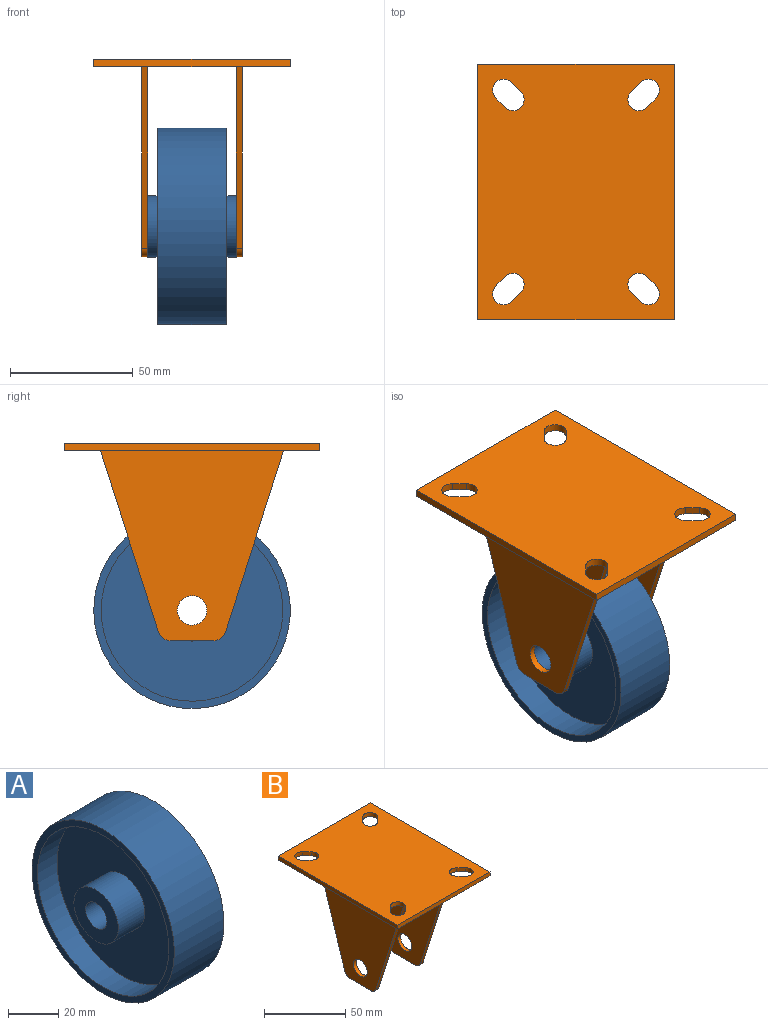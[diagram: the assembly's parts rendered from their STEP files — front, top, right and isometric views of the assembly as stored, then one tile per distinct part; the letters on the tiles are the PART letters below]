
ASSEMBLY  parts=2 mates=1
PART A: 12 faces, bbox 36x80x80 mm
  f0: cylinder r=40mm len=80mm, axis (-1,0,0), area 7037.2mm2, adj f1,f7
  f1: plane 80x80mm, normal (1,0,0), area 725.7mm2, adj f0,f2
  f2: cylinder r=37mm len=74mm, axis (1,0,0), area 2557.3mm2, adj f1,f3
  f3: plane 74x74mm, normal (1,0,0), area 3810mm2, adj f2,f4
  f4: cylinder r=12.5mm len=25mm, axis (-1,0,0), area 1178.1mm2, adj f3,f6
  f5: cylinder r=6mm len=36mm, axis (-1,0,0), area 1357.2mm2, adj f6,f11
  f6: plane 25x25mm, normal (1,0,0), area 377.8mm2, adj f4,f5
  f7: plane 80x80mm, normal (-1,0,0), area 725.7mm2, adj f0,f8
  f8: cylinder r=37mm len=74mm, axis (-1,0,0), area 2557.3mm2, adj f7,f9
  f9: plane 74x74mm, normal (-1,0,0), area 3810mm2, adj f8,f10
  f10: cylinder r=12.5mm len=25mm, axis (1,0,0), area 1178.1mm2, adj f9,f11
  f11: plane 25x25mm, normal (-1,0,0), area 377.8mm2, adj f5,f10
PART B: 38 faces, bbox 80x104x80.4 mm
  f0: plane 73.88x23.69mm, normal (0,0.95,-0.31), area 194mm2, adj f2,f3,f6,f36
  f1: plane 73.88x23.69mm, normal (0,-0.95,-0.31), area 194mm2, adj f2,f3,f4,f36
  f2: plane 77.35x74.61mm, normal (-1,0,0), area 3734.7mm2, adj f0,f1,f4,f5,f6,f7,f36
  f3: plane 77.35x74.61mm, normal (1,0,0), area 3734.7mm2, adj f0,f1,f4,f5,f6,f7,f36
  f4: cylinder r=5mm len=4.76mm, axis (1,0,0), area 15.8mm2, adj f1,f2,f3,f5
  f5: plane 17.71x2.5mm, normal (0,0,-1), area 44.3mm2, adj f2,f3,f4,f6
  f6: cylinder r=5mm len=4.76mm, axis (1,0,0), area 15.8mm2, adj f0,f2,f3,f5
  f7: cylinder r=6mm len=12mm, axis (1,0,0), area 94.2mm2, adj f2,f3
  f8: plane 73.88x23.69mm, normal (0,0.95,-0.31), area 194mm2, adj f10,f11,f14,f36
  f9: plane 73.88x23.69mm, normal (0,-0.95,-0.31), area 194mm2, adj f10,f11,f12,f36
  f10: plane 77.35x74.61mm, normal (1,0,0), area 3734.7mm2, adj f8,f9,f12,f13,f14,f15,f36
  f11: plane 77.35x74.61mm, normal (-1,0,0), area 3734.7mm2, adj f8,f9,f12,f13,f14,f15,f36
  f12: cylinder r=5mm len=4.76mm, axis (-1,0,0), area 15.8mm2, adj f9,f10,f11,f13
  f13: plane 17.71x2.5mm, normal (0,0,-1), area 44.3mm2, adj f10,f11,f12,f14
  f14: cylinder r=5mm len=4.76mm, axis (-1,0,0), area 15.8mm2, adj f8,f10,f11,f13
  f15: cylinder r=6mm len=12mm, axis (-1,0,0), area 94.2mm2, adj f10,f11
  f16: plane 3.89x3.89mm, normal (-0.71,0.71,0), area 16.5mm2, adj f17,f35,f36,f37
  f17: cylinder r=4.5mm len=7.68mm, axis (0,0,1), area 42.4mm2, adj f16,f18,f36,f37
  f18: plane 3.89x3.89mm, normal (0.71,-0.71,0), area 16.5mm2, adj f17,f35,f36,f37
  f19: plane 3.89x3.89mm, normal (-0.71,0.71,0), area 16.5mm2, adj f20,f31,f36,f37
  f20: cylinder r=4.5mm len=7.68mm, axis (0,0,1), area 42.4mm2, adj f19,f21,f36,f37
  f21: plane 3.89x3.89mm, normal (0.71,-0.71,0), area 16.5mm2, adj f20,f31,f36,f37
  f22: plane 104x3mm, normal (-1,0,0), area 312mm2, adj f23,f32,f36,f37
  f23: plane 80x3mm, normal (0,-1,0), area 240mm2, adj f22,f24,f36,f37
  f24: plane 104x3mm, normal (1,0,0), area 312mm2, adj f23,f32,f36,f37
  f25: cylinder r=4.5mm len=7.68mm, axis (0,0,1), area 42.4mm2, adj f26,f33,f36,f37
  f26: plane 3.89x3.89mm, normal (0.71,0.71,0), area 16.5mm2, adj f25,f27,f36,f37
  f27: cylinder r=4.5mm len=7.68mm, axis (0,0,1), area 42.4mm2, adj f26,f33,f36,f37
  f28: cylinder r=4.5mm len=7.68mm, axis (0,0,1), area 42.4mm2, adj f29,f34,f36,f37
  f29: plane 3.89x3.89mm, normal (-0.71,-0.71,0), area 16.5mm2, adj f28,f30,f36,f37
  f30: cylinder r=4.5mm len=7.68mm, axis (0,0,1), area 42.4mm2, adj f29,f34,f36,f37
  f31: cylinder r=4.5mm len=7.68mm, axis (0,0,1), area 42.4mm2, adj f19,f21,f36,f37
  f32: plane 80x3mm, normal (0,1,0), area 240mm2, adj f22,f24,f36,f37
  f33: plane 3.89x3.89mm, normal (-0.71,-0.71,0), area 16.5mm2, adj f25,f27,f36,f37
  f34: plane 3.89x3.89mm, normal (0.71,0.71,0), area 16.5mm2, adj f28,f30,f36,f37
  f35: cylinder r=4.5mm len=7.68mm, axis (0,0,1), area 42.4mm2, adj f16,f18,f36,f37
  f36: plane 104x80mm, normal (0,0,-1), area 7494.5mm2, adj f0,f1,f2,f3,f8,f9,f10,f11
  f37: plane 104x80mm, normal (0,0,1), area 7867.5mm2, adj f16,f17,f18,f19,f20,f21,f22,f23
PLACE A at identity
PLACE B at identity
MATE fastened B.f7 <-> A.f0  axis (-1,0,0) through (18,0,-68)mm
